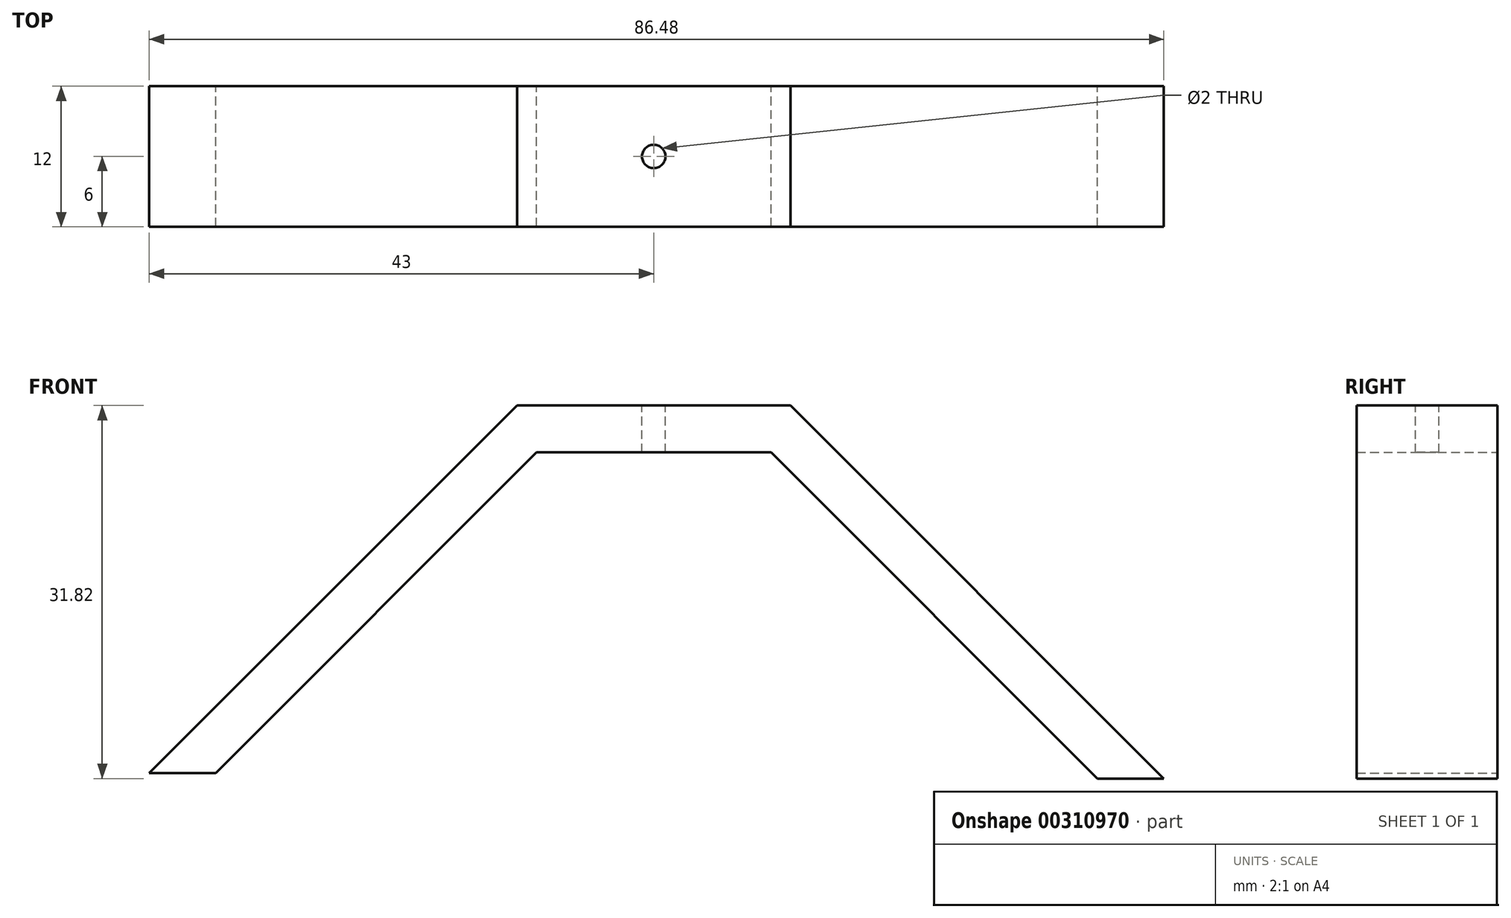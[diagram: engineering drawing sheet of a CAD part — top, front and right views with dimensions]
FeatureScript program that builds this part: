
annotation { "Feature Type Name" : "Feature", "Feature Type Description" : "" }
export const myFeature = defineFeature(function(context is Context, id is Id, definition is map)
    precondition{}
    {
        {
            var Q0;
            Q0=qCreatedBy(makeId("Front.planeOp"),FACE);
            var sketch = newSketch(context, id + "F0", { "sketchPlane" : qUnion([Q0])});
            skLineSegment(sketch, "E0", {"start": v(-10, 0) * mm, "end": v(10, 0) * mm});
            skLineSegment(sketch, "E1", {"start": v(-10, 0) * mm, "end": v(-37.34, -27.34) * mm});
            skLineSegment(sketch, "E2", {"start": v(10, 0) * mm, "end": v(37.82, -27.82) * mm});
            skLineSegment(sketch, "E3", {"start": v(-11.66, 4) * mm, "end": v(11.66, 4) * mm});
            skLineSegment(sketch, "E4", {"start": v(-11.66, 4) * mm, "end": v(-43, -27.34) * mm});
            skLineSegment(sketch, "E5", {"start": v(-43, -27.34) * mm, "end": v(-37.34, -27.34) * mm});
            skLineSegment(sketch, "E6", {"start": v(11.66, 4) * mm, "end": v(43.48, -27.82) * mm});
            skLineSegment(sketch, "E7", {"start": v(43.48, -27.82) * mm, "end": v(37.82, -27.82) * mm});
            skSolve(sketch);
        }
        {
            var Q0;
            Q0=makeQuery(id+"F0.imprint","IMPRINT",FACE,{"disambiguationData":[TD([[makeQuery(id+"F0.imprint","IMPRINT",EDGE,{"derivedFrom":sQuery(id+"F0.wireOp",EDGE,"E0")}),1.0]])]});
            extrude(context, id + "F1", {"entities" : qUnion([Q0]), "depth" : 12 * mm});
        }
        {
            var Q0;
            Q0=makeQuery(id+"F1.opExtrude","SWEPT_FACE",FACE,{"disambiguationData":[OSD([sQuery(id+"F0.wireOp",EDGE,"E3")])]});
            var sketch = newSketch(context, id + "F2", { "sketchPlane" : qUnion([Q0])});
            skCircle(sketch, "E8", {"center": v(0, -6) * mm, "radius": 1 * mm});
            skSolve(sketch);
        }
        {
            var Q0;
            Q0=makeQuery(id+"F2.imprint","IMPRINT",FACE,{"disambiguationData":[TD([[makeQuery(id+"F2.imprint","IMPRINT",EDGE,{"derivedFrom":sQuery(id+"F2.wireOp",EDGE,"E8")}),1.0]])]});
            extrude(context, id + "F3", {"entities" : qUnion([Q0]), "operationType" : NewBodyOperationType.REMOVE, "endBound" : BoundingType.THROUGH_ALL, "oppositeDirection" : true, "depth" : 25 * mm});
        }
    });
